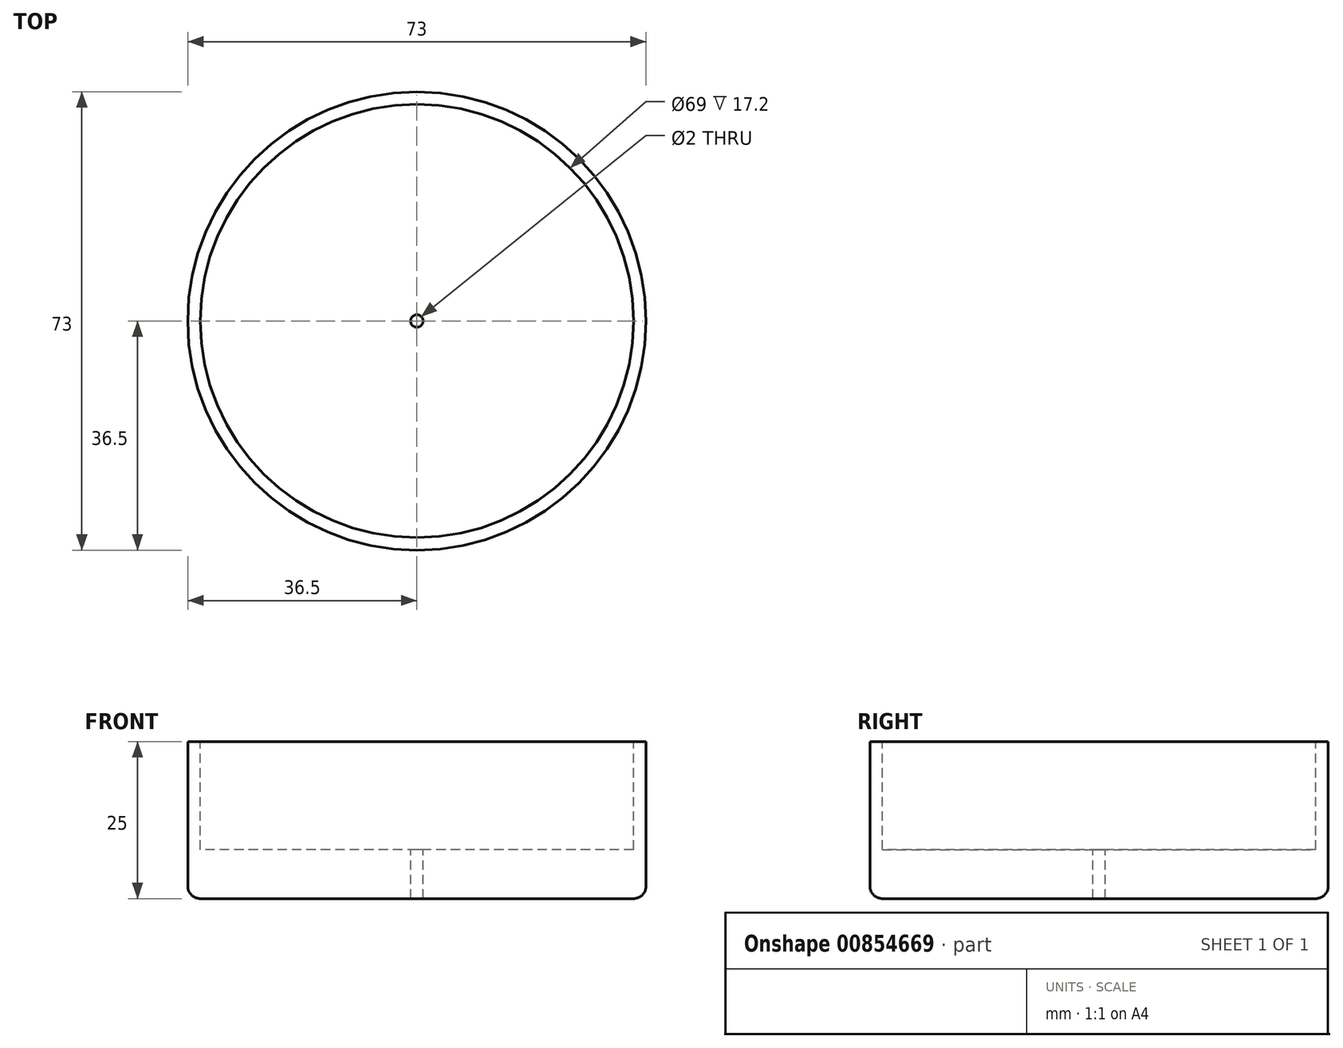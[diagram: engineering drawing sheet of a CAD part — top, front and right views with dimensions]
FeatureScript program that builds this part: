
annotation { "Feature Type Name" : "Feature", "Feature Type Description" : "" }
export const myFeature = defineFeature(function(context is Context, id is Id, definition is map)
    precondition{}
    {
        {
            var Q0;
            Q0=qCreatedBy(makeId("Top.planeOp"),FACE);
            var sketch = newSketch(context, id + "F0", { "sketchPlane" : qUnion([Q0])});
            skCircle(sketch, "E0", {"center": v(0, 0) * mm, "radius": 36.5 * mm});
            skSolve(sketch);
        }
        {
            var Q0;
            Q0 = qSketchRegion(id + "F0", true);
            extrude(context, id + "F1", {"entities" : qUnion([Q0]), "depth" : 25 * mm, "offsetDistance" : 25 * mm});
        }
        {
            var Q0;
            Q0=makeQuery(id+"F1.opExtrude","CAP_EDGE",EDGE,{"disambiguationData":[OSD([sQuery(id+"F0.wireOp",EDGE,"E0")])],"isStart":true});
            fillet(context, id + "F2", {"entities" : qUnion([Q0]), "radius" : 2 * mm, "tangentPropagation" : true, "allowEdgeOverflow" : false});
        }
        {
            var Q0;
            Q0=makeQuery(id+"F1.opExtrude","CAP_FACE",FACE,{"disambiguationData":[OSD([sQuery(id+"F0.wireOp",EDGE,"E0")])],"isStart":false});
            var sketch = newSketch(context, id + "F3", { "sketchPlane" : qUnion([Q0])});
            skCircle(sketch, "E1", {"center": v(0, 0) * mm, "radius": 34.5 * mm});
            skSolve(sketch);
        }
        {
            var Q0;
            Q0 = qSketchRegion(id + "F3", true);
            extrude(context, id + "F4", {"entities" : qUnion([Q0]), "operationType" : NewBodyOperationType.REMOVE, "oppositeDirection" : true, "depth" : 17.2 * mm, "offsetDistance" : 25 * mm});
        }
        {
            var Q0;
            Q0=makeQuery(id+"F4.boolean.opBoolean","COPY",FACE,{"derivedFrom":makeQuery(id+"F4.opExtrude","CAP_FACE",FACE,{"disambiguationData":[OSD([sQuery(id+"F3.wireOp",EDGE,"E1")])],"isStart":false})});
            var sketch = newSketch(context, id + "F5", { "sketchPlane" : qUnion([Q0])});
            skCircle(sketch, "E2", {"center": v(0, 0) * mm, "radius": 1 * mm});
            skSolve(sketch);
        }
        {
            var Q0;
            Q0 = qSketchRegion(id + "F5", true);
            extrude(context, id + "F6", {"entities" : qUnion([Q0]), "operationType" : NewBodyOperationType.REMOVE, "oppositeDirection" : true, "depth" : 25 * mm, "offsetDistance" : 25 * mm});
        }
    });
